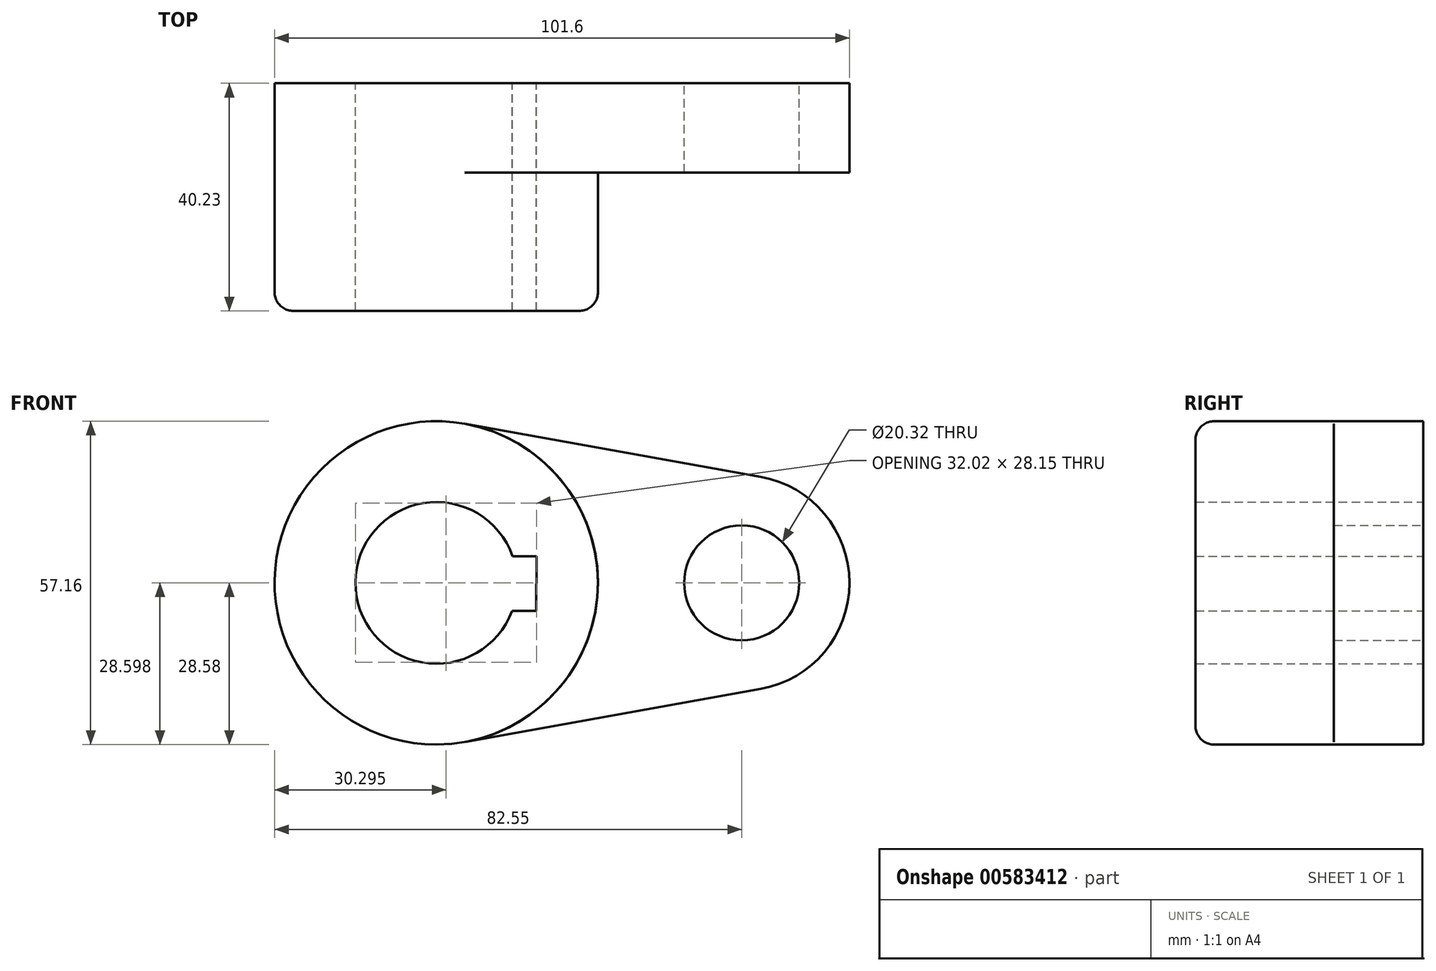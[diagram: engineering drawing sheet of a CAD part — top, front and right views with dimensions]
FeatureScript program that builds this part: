
annotation { "Feature Type Name" : "Feature", "Feature Type Description" : "" }
export const myFeature = defineFeature(function(context is Context, id is Id, definition is map)
    precondition{}
    {
        {
            var Q0;
            Q0=qCreatedBy(makeId("Front.planeOp"),FACE);
            var sketch = newSketch(context, id + "F0", { "sketchPlane" : qUnion([Q0])});
            skCircle(sketch, "E0", {"center": v(-53.98, 0) * mm, "radius": 28.58 * mm});
            skArc(sketch, "E1", {"start": v(-40.49, 4.72) * mm, "mid": v(-68.26, 0.1) * mm, "end": v(-40.56, -4.92) * mm});
            skCircle(sketch, "E2", {"center": v(-53.98, 0) * mm, "radius": 25.4 * mm});
            skCircle(sketch, "E3", {"center": v(0, 0) * mm, "radius": 10.16 * mm});
            skLineSegment(sketch, "E4.bottom", {"start": v(-40.49, 4.72) * mm, "end": v(-36.25, 4.73) * mm});
            skLineSegment(sketch, "E4.right", {"start": v(-36.25, 4.73) * mm, "end": v(-36.32, -4.92) * mm});
            skLineSegment(sketch, "E5", {"start": v(-36.32, -4.92) * mm, "end": v(-40.56, -4.92) * mm});
            skLineSegment(sketch, "E6", {"start": v(3.36, 18.75) * mm, "end": v(-48.93, 28.13) * mm});
            skArc(sketch, "E7", {"start": v(3.36, -18.75) * mm, "mid": v(19.05, 0) * mm, "end": v(3.36, 18.75) * mm});
            skLineSegment(sketch, "E8", {"start": v(3.36, 18.75) * mm, "end": v(3.36, -18.75) * mm});
            skLineSegment(sketch, "E9", {"start": v(-48.91, -28.12) * mm, "end": v(3.36, -18.75) * mm});
            skSolve(sketch);
        }
        {
            var Q0;
            Q0=makeQuery(id+"F0.imprint","IMPRINT",FACE,{"disambiguationData":[TD([[makeQuery(id+"F0.imprint","IMPRINT",EDGE,{"derivedFrom":sQuery(id+"F0.wireOp",EDGE,"E1")}),-1.0]])]});
            var Q1;
            Q1=makeQuery(id+"F0.imprint","IMPRINT",FACE,{"disambiguationData":[TD([[makeQuery(id+"F0.imprint","IMPRINT",EDGE,{"derivedFrom":sQuery(id+"F0.wireOp",EDGE,"E2")}),-1.0]])]});
            extrude(context, id + "F1", {"entities" : qUnion([Q0, Q1]), "depth" : 40.23 * mm, "offsetDistance" : 25.4 * mm});
        }
        {
            var Q0;
            {var subQ4=sQuery(id+"F0.wireOp",EDGE,"E7");Q0=makeQuery(id+"F0.imprint","IMPRINT",FACE,{"disambiguationData":[TD([[makeQuery(id+"F0.imprint","IMPRINT",EDGE,{"derivedFrom":subQ4}),1.0]])]});}
            var Q1;
            {var subQ0=sQuery(id+"F0.wireOp",EDGE,"E6");Q1=makeQuery(id+"F0.imprint","IMPRINT",FACE,{"disambiguationData":[TD([[makeQuery(id+"F0.imprint","IMPRINT",EDGE,{"derivedFrom":subQ0}),1.0]])]});}
            extrude(context, id + "F2", {"entities" : qUnion([Q0, Q1]), "operationType" : NewBodyOperationType.ADD, "depth" : 15.77 * mm, "offsetDistance" : 25.4 * mm});
        }
        {
            var Q0;
            Q0=makeQuery(id+"F1.opExtrude","CAP_EDGE",EDGE,{"disambiguationData":[OSD([sQuery(id+"F0.wireOp",EDGE,"E0")])],"isStart":false});
            fillet(context, id + "F3", {"entities" : qUnion([Q0]), "radius" : 3.3 * mm, "tangentPropagation" : true, "allowEdgeOverflow" : false});
        }
    });
